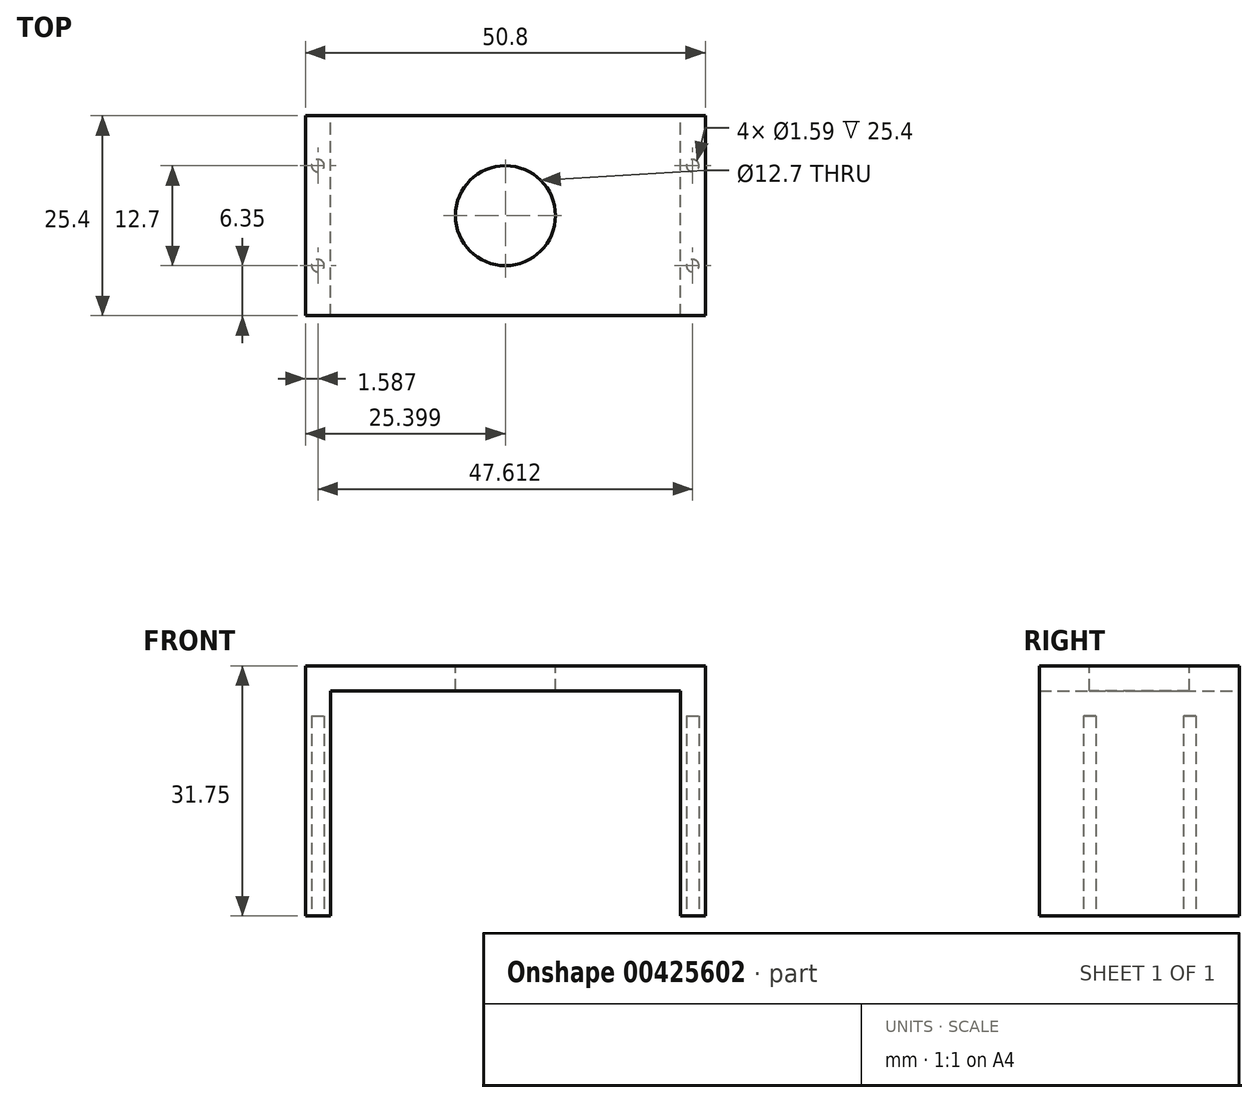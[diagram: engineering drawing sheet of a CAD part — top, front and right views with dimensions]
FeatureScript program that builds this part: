
annotation { "Feature Type Name" : "Feature", "Feature Type Description" : "" }
export const myFeature = defineFeature(function(context is Context, id is Id, definition is map)
    precondition{}
    {
        {
            var Q0;
            Q0=qCreatedBy(makeId("Front.planeOp"),FACE);
            var sketch = newSketch(context, id + "F0", { "sketchPlane" : qUnion([Q0])});
            skLineSegment(sketch, "E0", {"start": v(-13.93, -3.05) * mm, "end": v(-10.76, -3.05) * mm});
            skLineSegment(sketch, "E1", {"start": v(-10.76, -3.05) * mm, "end": v(-10.76, 25.52) * mm});
            skLineSegment(sketch, "E2", {"start": v(-10.76, 25.52) * mm, "end": v(33.7, 25.52) * mm});
            skLineSegment(sketch, "E3", {"start": v(33.7, 25.52) * mm, "end": v(33.7, -3.05) * mm});
            skLineSegment(sketch, "E4", {"start": v(33.7, -3.05) * mm, "end": v(36.87, -3.05) * mm});
            skLineSegment(sketch, "E5", {"start": v(36.87, -3.05) * mm, "end": v(36.87, 28.7) * mm});
            skLineSegment(sketch, "E6", {"start": v(36.87, 28.7) * mm, "end": v(-13.93, 28.7) * mm});
            skLineSegment(sketch, "E7", {"start": v(-13.93, 28.7) * mm, "end": v(-13.93, -3.05) * mm});
            skSolve(sketch);
        }
        {
            var Q0;
            Q0=makeQuery(id+"F0.imprint","IMPRINT",FACE,{"disambiguationData":[TD([[makeQuery(id+"F0.imprint","IMPRINT",EDGE,{"derivedFrom":sQuery(id+"F0.wireOp",EDGE,"E0")}),1.0]])]});
            extrude(context, id + "F1", {"entities" : qUnion([Q0]), "depth" : 25.4 * mm});
        }
        {
            var Q0;
            Q0=makeQuery(id+"F1.opExtrude","SWEPT_FACE",FACE,{"disambiguationData":[OSD([sQuery(id+"F0.wireOp",EDGE,"E6")])]});
            var sketch = newSketch(context, id + "F2", { "sketchPlane" : qUnion([Q0])});
            skCircle(sketch, "E8", {"center": v(11.47, -12.7) * mm, "radius": 6.35 * mm});
            skSolve(sketch);
        }
        {
            var Q0;
            Q0=makeQuery(id+"F2.imprint","IMPRINT",FACE,{"disambiguationData":[TD([[makeQuery(id+"F2.imprint","IMPRINT",EDGE,{"derivedFrom":sQuery(id+"F2.wireOp",EDGE,"E8")}),1.0]])]});
            extrude(context, id + "F3", {"entities" : qUnion([Q0]), "operationType" : NewBodyOperationType.REMOVE, "oppositeDirection" : true, "depth" : 25.4 * mm});
        }
        {
            var Q0;
            Q0=makeQuery(id+"F1.opExtrude","SWEPT_FACE",FACE,{"disambiguationData":[OSD([sQuery(id+"F0.wireOp",EDGE,"E4")])]});
            var sketch = newSketch(context, id + "F4", { "sketchPlane" : qUnion([Q0])});
            skCircle(sketch, "E9", {"center": v(-12.34, 19.05) * mm, "radius": 0.8 * mm});
            skCircle(sketch, "E10", {"center": v(-12.34, 6.35) * mm, "radius": 0.8 * mm});
            skSolve(sketch);
        }
        {
            var Q0;
            {var subQ0=sQuery(id+"F0.wireOp",EDGE,"E4");Q0=makeQuery(id+"F4.imprint","IMPRINT",FACE,{"disambiguationData":[TD([[makeQuery(id+"F4.imprint","IMPRINT",EDGE,{"derivedFrom":makeQuery(id+"F1.opExtrude","CAP_EDGE",EDGE,{"disambiguationData":[OSD([subQ0])],"isStart":true})}),1.0]])]});}
            var sketch = newSketch(context, id + "F5", { "sketchPlane" : qUnion([Q0])});
            skCircle(sketch, "E11", {"center": v(35.27, 19.05) * mm, "radius": 0.8 * mm});
            skCircle(sketch, "E12", {"center": v(35.27, 6.35) * mm, "radius": 0.8 * mm});
            skSolve(sketch);
        }
        {
            var Q0;
            Q0=makeQuery(id+"F4.imprint","IMPRINT",FACE,{"disambiguationData":[TD([[makeQuery(id+"F4.imprint","IMPRINT",EDGE,{"derivedFrom":sQuery(id+"F4.wireOp",EDGE,"E9")}),1.0]])]});
            var Q1;
            Q1=makeQuery(id+"F4.imprint","IMPRINT",FACE,{"disambiguationData":[TD([[makeQuery(id+"F4.imprint","IMPRINT",EDGE,{"derivedFrom":sQuery(id+"F4.wireOp",EDGE,"E10")}),1.0]])]});
            extrude(context, id + "F6", {"entities" : qUnion([Q0, Q1]), "operationType" : NewBodyOperationType.REMOVE, "oppositeDirection" : true, "depth" : 25.4 * mm});
        }
        {
            var Q0;
            Q0=makeQuery(id+"F5.imprint","IMPRINT",FACE,{"disambiguationData":[TD([[makeQuery(id+"F5.imprint","IMPRINT",EDGE,{"derivedFrom":sQuery(id+"F5.wireOp",EDGE,"E11")}),1.0]])]});
            var Q1;
            Q1=makeQuery(id+"F5.imprint","IMPRINT",FACE,{"disambiguationData":[TD([[makeQuery(id+"F5.imprint","IMPRINT",EDGE,{"derivedFrom":sQuery(id+"F5.wireOp",EDGE,"E12")}),1.0]])]});
            extrude(context, id + "F7", {"entities" : qUnion([Q0, Q1]), "operationType" : NewBodyOperationType.REMOVE, "oppositeDirection" : true, "depth" : 25.4 * mm});
        }
    });
